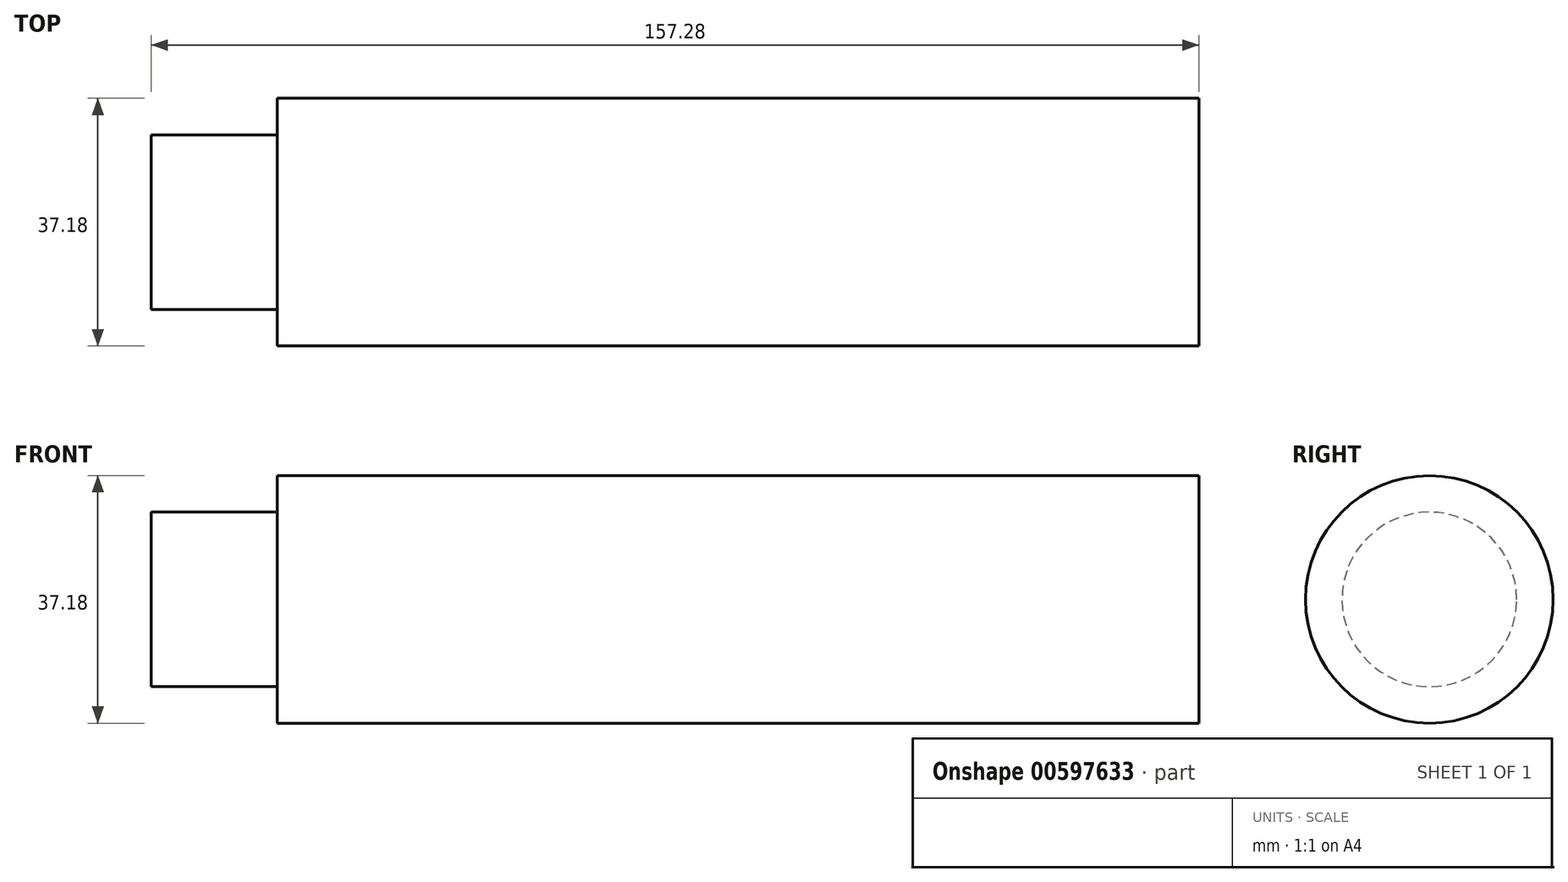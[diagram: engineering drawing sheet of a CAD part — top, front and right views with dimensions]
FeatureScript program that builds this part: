
annotation { "Feature Type Name" : "Feature", "Feature Type Description" : "" }
export const myFeature = defineFeature(function(context is Context, id is Id, definition is map)
    precondition{}
    {
        {
            var Q0;
            Q0=qCreatedBy(makeId("Front.planeOp"),FACE);
            var sketch = newSketch(context, id + "F0", { "sketchPlane" : qUnion([Q0])});
            skLineSegment(sketch, "E0", {"start": v(-50.75, 18.6) * mm, "end": v(87.63, 18.6) * mm});
            skLineSegment(sketch, "E1", {"start": v(87.63, 18.6) * mm, "end": v(87.63, 0) * mm});
            skLineSegment(sketch, "E2", {"start": v(87.63, 0) * mm, "end": v(-69.65, 0) * mm});
            skLineSegment(sketch, "E3", {"start": v(-69.65, 0) * mm, "end": v(-69.65, 13.1) * mm});
            skLineSegment(sketch, "E4", {"start": v(-69.65, 13.1) * mm, "end": v(-50.75, 13.1) * mm});
            skLineSegment(sketch, "E5", {"start": v(-50.75, 13.1) * mm, "end": v(-50.75, 18.6) * mm});
            skSolve(sketch);
        }
        {
            var Q0;
            Q0=makeQuery(id+"F0.imprint","IMPRINT",FACE,{"disambiguationData":[TD([[makeQuery(id+"F0.imprint","IMPRINT",EDGE,{"derivedFrom":sQuery(id+"F0.wireOp",EDGE,"E0")}),-1.0]])]});
            var Q1;
            Q1=sQuery(id+"F0.wireOp",EDGE,"E2");
            revolve(context, id + "F1", {"entities" : qUnion([Q0]), "axis" : qUnion([Q1]), "revolveType" : RevolveType.FULL});
        }
    });
